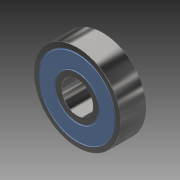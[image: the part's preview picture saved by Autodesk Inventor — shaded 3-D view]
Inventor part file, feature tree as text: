
AUTODESK INVENTOR PART (.ipt)
format: ipt  version: 2018 (Build 220112000, 112)  size: 198,656 bytes
history: native  units: in
note: dims shown in document units (in); Inventor stores cm internally (conversion verified against a paired STEP export)
features: sketch x2, extrude x1, fillet x1, revolve x1, plane x1, mirror x1
ambient origin geometry x8: Origin, YZ Plane, XZ Plane, XY Plane, X Axis, Y Axis, Z Axis, Center Point
bodies: Solid1 (feature_tree)
feature tree (7):
  extrude  "Extrusion1"  Depth=0.5512in
  fillet  "Fillet1"  Radius=0.5512in
  revolve  "Revolution1"  Angle=90.0deg
  plane  "Work Plane1"
  mirror  "Mirror1"
  sketch  "Sketch1"  dims[d0=0.6693in d1=1.8504in d2=0.5512in d3=0.0in]
  sketch  "Sketch2"  dims[d4=0.0118in d5=90.0deg]
